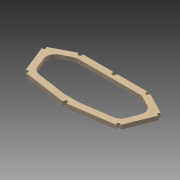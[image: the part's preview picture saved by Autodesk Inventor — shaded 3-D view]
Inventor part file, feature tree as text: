
AUTODESK INVENTOR PART (.ipt)
format: ipt  version: 2015 (Build 190159000, 159)  size: 199,168 bytes
history: native  units: mm
features: fillet x12, hole x5, extrude x2, sketch x2, mirror x1
ambient origin geometry x8: Origin, YZ Plane, XZ Plane, XY Plane, X Axis, Y Axis, Z Axis, Center Point
bodies: Solid4 (feature_tree)
feature tree (22):
  extrude  "Extrusion4"  Depth=228.6mm
  hole  "Hole2"  [1 undecoded]
  hole  "Hole3"  [1 undecoded]
  hole  "Hole4"  [1 undecoded]
  hole  "Hole5"  [1 undecoded]
  hole  "Hole6"  [1 undecoded]
  fillet  "Fillet6"  Radius=18.0mm
  fillet  "Fillet7"  Radius=5.0mm
  fillet  "Fillet8"  Radius=3.0mm
  fillet  "Fillet9"  Radius=3.0mm
  fillet  "Fillet10"  Radius=1.0mm
  fillet  "Fillet11"  Radius=1.0mm
  fillet  "Fillet12"  Radius=3.5mm
  fillet  "Fillet13"  Radius=1.0mm
  extrude  "Extrusion5"  Depth=1.0mm
  fillet  "Fillet14"  Radius=28.0mm
  fillet  "Fillet15"  Radius=28.0mm
  fillet  "Fillet16"  Radius=28.0mm
  fillet  "Fillet17"  Radius=28.0mm
  mirror  "Mirror3"
  sketch  "Sketch1"  dims[d9=228.6mm d11=263.0424mm]
  sketch  "Sketch4"  dims[d15=170.9928mm d20=207.5688mm d22=32.6136mm d39=152.4mm d41=0.0mm d42=2.1336mm d98=18.0mm d99=0.0mm d161=10.0mm d162=10.0mm d102=15.0mm d103=6.0mm d104=3.023mm d105=2.0mm d106=14.3117mm d107=8.0mm d108=20.594885mm d163=10.0mm d164=10.0mm d111=15.0mm d112=6.0mm d113=3.023mm d114=2.0mm d115=14.3117mm d116=8.0mm d117=20.594885mm d165=10.0mm d166=10.0mm d124=15.0mm d125=6.0mm d126=3.023mm d127=2.0mm d128=14.3117mm d129=8.0mm d130=20.594885mm d157=10.0mm d158=10.0mm d133=15.0mm d134=6.0mm d135=3.023mm d136=2.0mm d137=14.3117mm d138=8.0mm d139=20.594885mm d167=10.0mm d168=10.0mm d150=15.0mm d151=6.0mm d152=4.0mm d153=2.0mm d154=90.0deg d155=8.0mm d156=20.594885mm d159=5.0mm d160=3.0mm d169=3.0mm d170=1.0mm d171=1.0mm d172=3.5mm d173=1.0mm d174=1.0mm d175=28.0mm d176=28.0mm d177=28.0mm d178=28.0mm d179=30.0mm d180=10.0mm d181=0.0mm d182=40.0mm d183=40.0mm d184=40.0mm d185=40.0mm]
note: 5 required parameter values undecoded (feature->parameter linkage not recoverable at this tier; creation-order binding heuristic only, values carry confidence <= 0.55)
